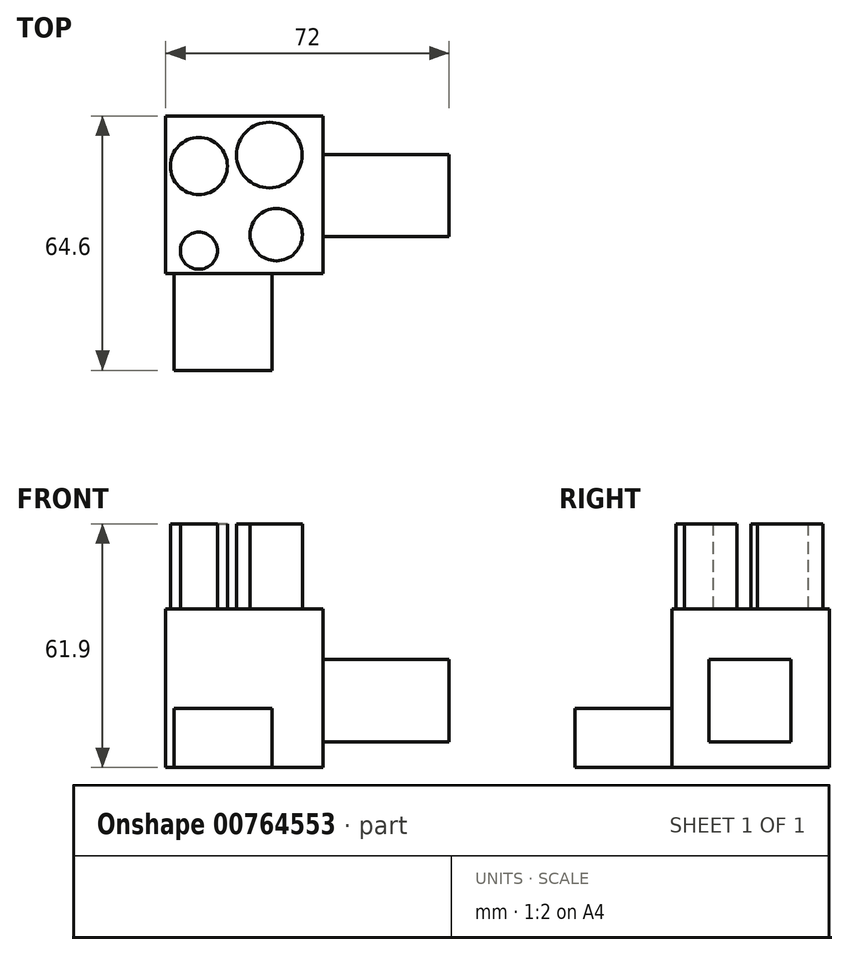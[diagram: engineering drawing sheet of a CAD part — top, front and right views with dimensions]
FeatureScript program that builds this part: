
annotation { "Feature Type Name" : "Feature", "Feature Type Description" : "" }
export const myFeature = defineFeature(function(context is Context, id is Id, definition is map)
    precondition{}
    {
        {
            var Q0;
            Q0=qCreatedBy(makeId("Top.planeOp"),FACE);
            var sketch = newSketch(context, id + "F0", { "sketchPlane" : qUnion([Q0])});
            skLineSegment(sketch, "E0.bottom", {"start": v(-51.88, 47.88) * mm, "end": v(-11.88, 47.88) * mm});
            skLineSegment(sketch, "E0.top", {"start": v(-51.88, 7.88) * mm, "end": v(-11.88, 7.88) * mm});
            skLineSegment(sketch, "E0.left", {"start": v(-51.88, 47.88) * mm, "end": v(-51.88, 7.88) * mm});
            skLineSegment(sketch, "E0.right", {"start": v(-11.88, 47.88) * mm, "end": v(-11.88, 7.88) * mm});
            skSolve(sketch);
        }
        {
            var Q0;
            Q0=makeQuery(id+"F0.imprint","IMPRINT",FACE,{"disambiguationData":[TD([[makeQuery(id+"F0.imprint","IMPRINT",EDGE,{"derivedFrom":sQuery(id+"F0.wireOp",EDGE,"E0.bottom")}),-1.0]])]});
            extrude(context, id + "F1", {"entities" : qUnion([Q0]), "depth" : 40.3 * mm, "offsetDistance" : 25 * mm});
        }
        {
            var Q0;
            Q0=makeQuery(id+"F1.opExtrude","SWEPT_FACE",FACE,{"disambiguationData":[OSD([sQuery(id+"F0.wireOp",EDGE,"E0.top")])]});
            var sketch = newSketch(context, id + "F2", { "sketchPlane" : qUnion([Q0])});
            skLineSegment(sketch, "E1.bottom", {"start": v(-49.81, 15) * mm, "end": v(-24.81, 15) * mm});
            skLineSegment(sketch, "E1.top", {"start": v(-49.81, 0) * mm, "end": v(-24.81, 0) * mm});
            skLineSegment(sketch, "E1.left", {"start": v(-49.81, 15) * mm, "end": v(-49.81, 0) * mm});
            skLineSegment(sketch, "E1.right", {"start": v(-24.81, 15) * mm, "end": v(-24.81, 0) * mm});
            skLineSegment(sketch, "E2.bottom", {"start": v(-99.35, -7.76) * mm, "end": v(-106.82, -7.76) * mm});
            skLineSegment(sketch, "E2.top", {"start": v(-99.35, -8.33) * mm, "end": v(-106.82, -8.33) * mm});
            skLineSegment(sketch, "E2.left", {"start": v(-99.35, -7.76) * mm, "end": v(-99.35, -8.33) * mm});
            skLineSegment(sketch, "E2.right", {"start": v(-106.82, -7.76) * mm, "end": v(-106.82, -8.33) * mm});
            skSolve(sketch);
        }
        {
            var Q0;
            Q0=makeQuery(id+"F2.imprint","IMPRINT",FACE,{"disambiguationData":[TD([[makeQuery(id+"F2.imprint","IMPRINT",EDGE,{"derivedFrom":sQuery(id+"F2.wireOp",EDGE,"E1.bottom")}),-1.0]])]});
            extrude(context, id + "F3", {"entities" : qUnion([Q0]), "operationType" : NewBodyOperationType.ADD, "depth" : 24.6 * mm, "offsetDistance" : 25 * mm});
        }
        {
            var Q0;
            Q0=makeQuery(id+"F1.opExtrude","SWEPT_FACE",FACE,{"disambiguationData":[OSD([sQuery(id+"F0.wireOp",EDGE,"E0.right")])]});
            var sketch = newSketch(context, id + "F4", { "sketchPlane" : qUnion([Q0])});
            skSolve(sketch);
        }
        {
            var Q0;
            {var subQ0=sQuery(id+"F0.wireOp",EDGE,"E0.right");Q0=makeQuery(id+"F4.imprint","IMPRINT",FACE,{"disambiguationData":[TD([[makeQuery(id+"F4.imprint","IMPRINT",EDGE,{"derivedFrom":makeQuery(id+"F1.opExtrude","CAP_EDGE",EDGE,{"disambiguationData":[OSD([subQ0])],"isStart":true})}),-1.0]])]});}
            var sketch = newSketch(context, id + "F5", { "sketchPlane" : qUnion([Q0])});
            skSolve(sketch);
        }
        {
            var Q0;
            {var subQ0=sQuery(id+"F0.wireOp",EDGE,"E0.right");Q0=makeQuery(id+"F5.imprint","IMPRINT",FACE,{"disambiguationData":[TD([[makeQuery(id+"F5.imprint","IMPRINT",EDGE,{"derivedFrom":makeQuery(id+"F4.imprint","IMPRINT",EDGE,{"derivedFrom":makeQuery(id+"F1.opExtrude","CAP_EDGE",EDGE,{"disambiguationData":[OSD([subQ0])],"isStart":true})})}),-1.0]])]});}
            var sketch = newSketch(context, id + "F6", { "sketchPlane" : qUnion([Q0])});
            skLineSegment(sketch, "E3.bottom", {"start": v(17.31, 27.5) * mm, "end": v(38.09, 27.5) * mm});
            skLineSegment(sketch, "E3.top", {"start": v(17.31, 6.49) * mm, "end": v(38.09, 6.49) * mm});
            skLineSegment(sketch, "E3.left", {"start": v(17.31, 27.5) * mm, "end": v(17.31, 6.49) * mm});
            skLineSegment(sketch, "E3.right", {"start": v(38.09, 27.5) * mm, "end": v(38.09, 6.49) * mm});
            skSolve(sketch);
        }
        {
            var Q0;
            Q0 = qSketchRegion(id + "F6", true);
            extrude(context, id + "F7", {"entities" : qUnion([Q0]), "operationType" : NewBodyOperationType.ADD, "depth" : 32 * mm, "offsetDistance" : 25 * mm});
        }
        {
            var Q0;
            Q0=makeQuery(id+"F1.opExtrude","CAP_FACE",FACE,{"disambiguationData":[OSD([sQuery(id+"F0.wireOp",EDGE,"E0.bottom"),sQuery(id+"F0.wireOp",EDGE,"E0.top"),sQuery(id+"F0.wireOp",EDGE,"E0.left"),sQuery(id+"F0.wireOp",EDGE,"E0.right")])],"isStart":false});
            var sketch = newSketch(context, id + "F8", { "sketchPlane" : qUnion([Q0])});
            skCircle(sketch, "E4", {"center": v(-43.44, 35.18) * mm, "radius": 7.25 * mm});
            skCircle(sketch, "E5", {"center": v(-23.78, 17.74) * mm, "radius": 6.64 * mm});
            skCircle(sketch, "E6", {"center": v(-25.53, 37.98) * mm, "radius": 8.33 * mm});
            skCircle(sketch, "E7", {"center": v(-43.44, 13.67) * mm, "radius": 4.7 * mm});
            skSolve(sketch);
        }
        {
            var Q0;
            Q0 = qSketchRegion(id + "F8", true);
            extrude(context, id + "F9", {"entities" : qUnion([Q0]), "operationType" : NewBodyOperationType.ADD, "depth" : 21.6 * mm, "offsetDistance" : 25 * mm});
        }
    });
